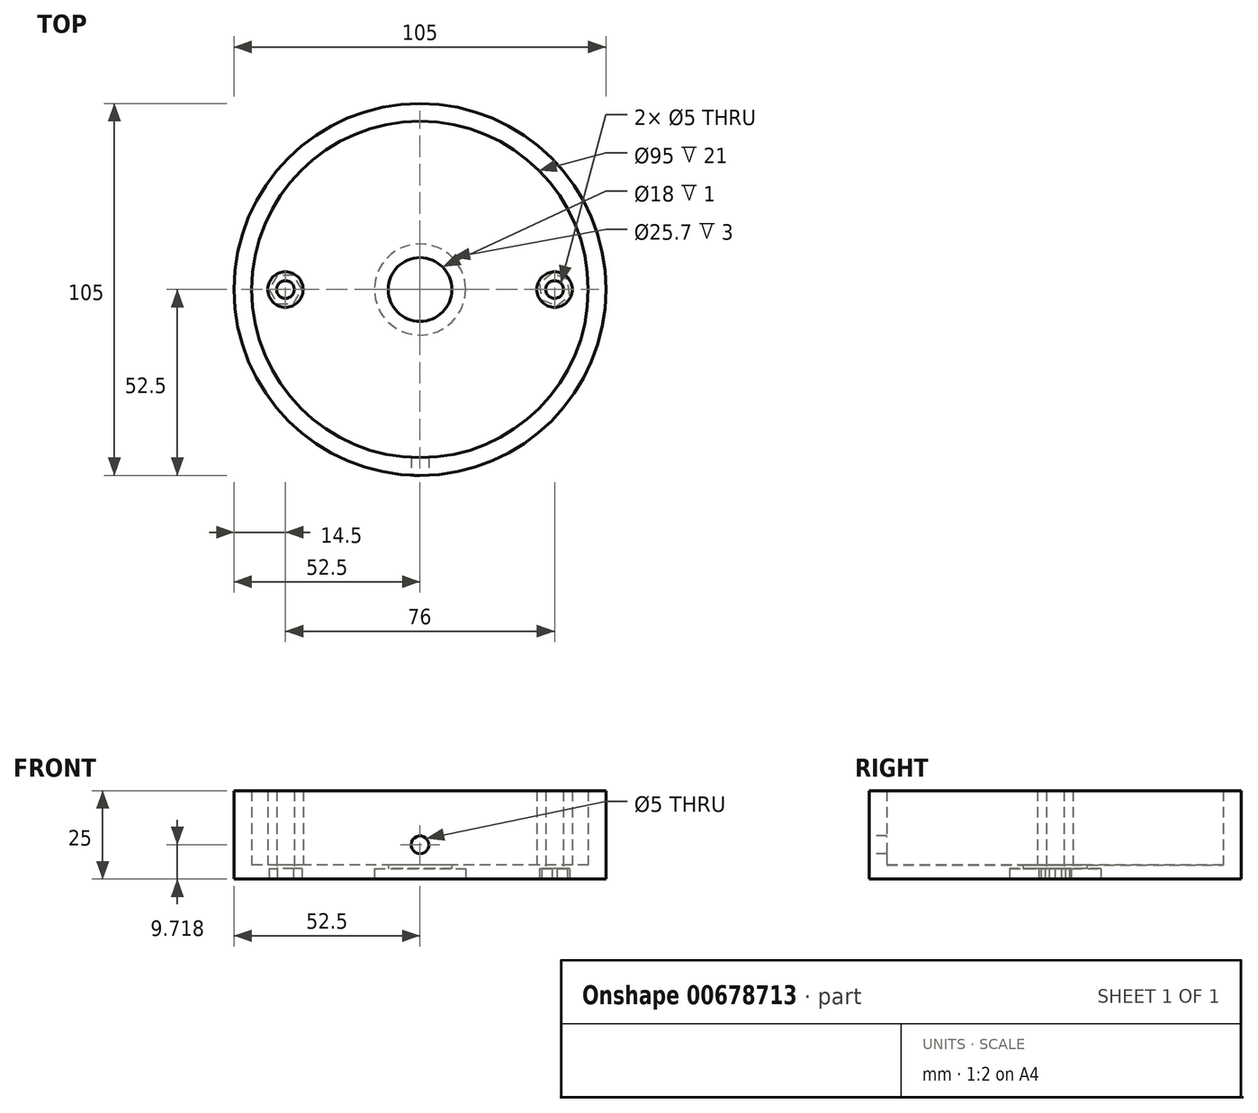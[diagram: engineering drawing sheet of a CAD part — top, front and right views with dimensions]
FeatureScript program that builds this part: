
annotation { "Feature Type Name" : "Feature", "Feature Type Description" : "" }
export const myFeature = defineFeature(function(context is Context, id is Id, definition is map)
    precondition{}
    {
        {
            var Q0;
            Q0=qCreatedBy(makeId("Top.planeOp"),FACE);
            var sketch = newSketch(context, id + "F0", { "sketchPlane" : qUnion([Q0])});
            skCircle(sketch, "E0", {"center": v(0, 0) * mm, "radius": 47.5 * mm});
            skCircle(sketch, "E1", {"center": v(0, 0) * mm, "radius": 52.5 * mm});
            skCircle(sketch, "E2", {"center": v(0, 0) * mm, "radius": 9 * mm});
            skPoint(sketch, "E3", {"position": v(38, 0) * mm});
            skCircle(sketch, "E4", {"center": v(38, 0) * mm, "radius": 2.5 * mm});
            skCircle(sketch, "E5", {"center": v(-38, 0) * mm, "radius": 2.5 * mm});
            skPoint(sketch, "E6", {"position": v(0, -30) * mm});
            skSolve(sketch);
        }
        {
            var Q0;
            Q0=makeQuery(id+"F0.imprint","IMPRINT",FACE,{"disambiguationData":[TD([[makeQuery(id+"F0.imprint","IMPRINT",EDGE,{"derivedFrom":sQuery(id+"F0.wireOp",EDGE,"E0")}),1.0]])]});
            extrude(context, id + "F1", {"entities" : qUnion([Q0]), "depth" : 4 * mm, "offsetDistance" : 25 * mm});
        }
        {
            var Q0;
            Q0=makeQuery(id+"F0.imprint","IMPRINT",FACE,{"disambiguationData":[TD([[makeQuery(id+"F0.imprint","IMPRINT",EDGE,{"derivedFrom":sQuery(id+"F0.wireOp",EDGE,"E0")}),-1.0]])]});
            extrude(context, id + "F2", {"entities" : qUnion([Q0]), "operationType" : NewBodyOperationType.ADD, "depth" : 22 * mm, "offsetDistance" : 25 * mm});
        }
        {
            var Q0;
            Q0 = qSketchRegion(id + "F0", true);
            extrude(context, id + "F3", {"entities" : qUnion([Q0]), "operationType" : NewBodyOperationType.ADD, "depth" : 25 * mm, "offsetDistance" : 25 * mm});
        }
        {
            var Q0;
            {var subQ0=sQuery(id+"F0.wireOp",EDGE,"KxPcmW6f-jrK5-NJJ2-CGSX-odAfUIyHA8Hz");var subQ1=sQuery(id+"F0.wireOp",EDGE,"Ce3efajX-mTEG-fQcQ-4AWC-PIJuVlCcTGQe");var subQ2=sQuery(id+"F0.wireOp",EDGE,"BphFqhMG-zdux-vk7n-OLHF-6ssDePMP9lv5");var subQ3=sQuery(id+"F0.wireOp",EDGE,"E0");Q0=makeQuery(id+"FwEDGeEJbmtDzLu_0.boolean.opBoolean","MERGE",FACE,{"derivedFrom":[makeQuery(id+"F2.boolean.opBoolean","MERGE",FACE,{"derivedFrom":[makeQuery(id+"F1.opExtrude","CAP_FACE",FACE,{"disambiguationData":[OSD([subQ3,sQuery(id+"F0.wireOp",EDGE,"B8NBj5N8-SaxT-broy-7EAl-QKT3yiHgvJLJ"),subQ2,subQ1,subQ0])],"isStart":true}),makeQuery(id+"F2.opExtrude","CAP_FACE",FACE,{"disambiguationData":[OSD([subQ3,sQuery(id+"F0.wireOp",EDGE,"E1")])],"isStart":true})]}),makeQuery(id+"FwEDGeEJbmtDzLu_0.opExtrude","CAP_FACE",FACE,{"disambiguationData":[OSD([sQuery(id+"F0.wireOp",EDGE,"WK8yWc9G-alHI-a11c-cyK7-Gcr48cerju4L"),subQ2])],"isStart":true}),makeQuery(id+"FwEDGeEJbmtDzLu_0.opExtrude","CAP_FACE",FACE,{"disambiguationData":[OSD([sQuery(id+"F0.wireOp",EDGE,"opKP8o53-cgpy-PRBC-jVus-ZTeZxwGO5yKw"),subQ1])],"isStart":true}),makeQuery(id+"FwEDGeEJbmtDzLu_0.opExtrude","CAP_FACE",FACE,{"disambiguationData":[OSD([sQuery(id+"F0.wireOp",EDGE,"vjQTa54q-FzXU-Qp47-7nQK-FbvYVxZVb2CL"),subQ0])],"isStart":true})]});}
            var sketch = newSketch(context, id + "F4", { "sketchPlane" : qUnion([Q0])});
            skSolve(sketch);
        }
        {
            var Q0;
            {var subQ0=sQuery(id+"F0.wireOp",EDGE,"KxPcmW6f-jrK5-NJJ2-CGSX-odAfUIyHA8Hz");var subQ1=sQuery(id+"F0.wireOp",EDGE,"Ce3efajX-mTEG-fQcQ-4AWC-PIJuVlCcTGQe");var subQ2=sQuery(id+"F0.wireOp",EDGE,"BphFqhMG-zdux-vk7n-OLHF-6ssDePMP9lv5");var subQ3=sQuery(id+"F0.wireOp",EDGE,"E0");Q0=makeQuery(id+"FwEDGeEJbmtDzLu_0.boolean.opBoolean","MERGE",FACE,{"derivedFrom":[makeQuery(id+"F2.boolean.opBoolean","MERGE",FACE,{"derivedFrom":[makeQuery(id+"F1.opExtrude","CAP_FACE",FACE,{"disambiguationData":[OSD([subQ3,sQuery(id+"F0.wireOp",EDGE,"B8NBj5N8-SaxT-broy-7EAl-QKT3yiHgvJLJ"),subQ2,subQ1,subQ0])],"isStart":true}),makeQuery(id+"F2.opExtrude","CAP_FACE",FACE,{"disambiguationData":[OSD([subQ3,sQuery(id+"F0.wireOp",EDGE,"E1")])],"isStart":true})]}),makeQuery(id+"FwEDGeEJbmtDzLu_0.opExtrude","CAP_FACE",FACE,{"disambiguationData":[OSD([sQuery(id+"F0.wireOp",EDGE,"WK8yWc9G-alHI-a11c-cyK7-Gcr48cerju4L"),subQ2])],"isStart":true}),makeQuery(id+"FwEDGeEJbmtDzLu_0.opExtrude","CAP_FACE",FACE,{"disambiguationData":[OSD([sQuery(id+"F0.wireOp",EDGE,"opKP8o53-cgpy-PRBC-jVus-ZTeZxwGO5yKw"),subQ1])],"isStart":true}),makeQuery(id+"FwEDGeEJbmtDzLu_0.opExtrude","CAP_FACE",FACE,{"disambiguationData":[OSD([sQuery(id+"F0.wireOp",EDGE,"vjQTa54q-FzXU-Qp47-7nQK-FbvYVxZVb2CL"),subQ0])],"isStart":true})]});}
            var sketch = newSketch(context, id + "F5", { "sketchPlane" : qUnion([Q0])});
            skCircle(sketch, "E7", {"center": v(0, 0) * mm, "radius": 12.85 * mm});
            skSolve(sketch);
        }
        {
            var Q0;
            Q0=makeQuery(id+"F5.imprint","IMPRINT",FACE,{"disambiguationData":[TD([[makeQuery(id+"F5.imprint","IMPRINT",EDGE,{"derivedFrom":sQuery(id+"F5.wireOp",EDGE,"E7")}),1.0]])]});
            extrude(context, id + "F6", {"entities" : qUnion([Q0]), "operationType" : NewBodyOperationType.REMOVE, "oppositeDirection" : true, "depth" : 3 * mm, "offsetDistance" : 25 * mm});
        }
        {
            var Q0;
            Q0=makeQuery(id+"F4.imprint","IMPRINT",FACE,{"disambiguationData":[TD([[makeQuery(id+"F4.imprint","IMPRINT",EDGE,{"derivedFrom":makeQuery(id+"F1.opExtrude","CAP_EDGE",EDGE,{"disambiguationData":[OSD([sQuery(id+"F0.wireOp",EDGE,"E2")])],"isStart":true})}),1.0]])]});
            var sketch = newSketch(context, id + "F7", { "sketchPlane" : qUnion([Q0])});
            skPoint(sketch, "E8", {"position": v(-38, 0) * mm});
            skPoint(sketch, "E9", {"position": v(0, 0) * mm});
            skPoint(sketch, "E10", {"position": v(38, 0) * mm});
            skLineSegment(sketch, "E11.0", {"start": v(-35.7, -4) * mm, "end": v(-40.3, -4) * mm});
            skLineSegment(sketch, "E11.1", {"start": v(-40.3, -4) * mm, "end": v(-42.62, 0) * mm});
            skLineSegment(sketch, "E11.2", {"start": v(-42.62, 0) * mm, "end": v(-40.3, 4) * mm});
            skLineSegment(sketch, "E11.3", {"start": v(-40.3, 4) * mm, "end": v(-35.7, 4) * mm});
            skLineSegment(sketch, "E11.4", {"start": v(-35.7, 4) * mm, "end": v(-33.38, 0) * mm});
            skLineSegment(sketch, "E11.5", {"start": v(-33.38, 0) * mm, "end": v(-35.7, -4) * mm});
            skPoint(sketch, "E11.0.midPoint", {"position": v(-38, -4) * mm});
            skLineSegment(sketch, "E12.0", {"start": v(41.62, -2.87) * mm, "end": v(37.32, -4.57) * mm});
            skLineSegment(sketch, "E12.1", {"start": v(37.32, -4.57) * mm, "end": v(33.7, -1.7) * mm});
            skLineSegment(sketch, "E12.2", {"start": v(33.7, -1.7) * mm, "end": v(34.38, 2.87) * mm});
            skLineSegment(sketch, "E12.3", {"start": v(34.38, 2.87) * mm, "end": v(38.68, 4.57) * mm});
            skLineSegment(sketch, "E12.4", {"start": v(38.68, 4.57) * mm, "end": v(42.3, 1.7) * mm});
            skLineSegment(sketch, "E12.5", {"start": v(42.3, 1.7) * mm, "end": v(41.62, -2.87) * mm});
            skPoint(sketch, "E12.0.midPoint", {"position": v(39.47, -3.72) * mm});
            skSolve(sketch);
        }
        {
            var Q0;
            Q0=makeQuery(id+"F7.imprint","IMPRINT",FACE,{"disambiguationData":[TD([[makeQuery(id+"F7.imprint","IMPRINT",EDGE,{"derivedFrom":sQuery(id+"F7.wireOp",EDGE,"E12.0")}),-1.0]])]});
            var Q1;
            Q1=makeQuery(id+"F7.imprint","IMPRINT",FACE,{"disambiguationData":[TD([[makeQuery(id+"F7.imprint","IMPRINT",EDGE,{"derivedFrom":sQuery(id+"F7.wireOp",EDGE,"E11.0")}),-1.0]])]});
            extrude(context, id + "F8", {"entities" : qUnion([Q0, Q1]), "operationType" : NewBodyOperationType.REMOVE, "oppositeDirection" : true, "depth" : 3 * mm, "offsetDistance" : 25 * mm});
        }
        {
            var Q0;
            Q0=makeQuery(id+"F1.opExtrude","CAP_FACE",FACE,{"disambiguationData":[OSD([sQuery(id+"F0.wireOp",EDGE,"E0"),sQuery(id+"F0.wireOp",EDGE,"E2"),sQuery(id+"F0.wireOp",EDGE,"E4"),sQuery(id+"F0.wireOp",EDGE,"E5")])],"isStart":false});
            var sketch = newSketch(context, id + "F9", { "sketchPlane" : qUnion([Q0])});
            skCircle(sketch, "E13", {"center": v(-38, 0) * mm, "radius": 5 * mm});
            skCircle(sketch, "E14", {"center": v(38, 0) * mm, "radius": 5 * mm});
            skSolve(sketch);
        }
        {
            var Q0;
            Q0=makeQuery(id+"F9.imprint","IMPRINT",FACE,{"disambiguationData":[TD([[makeQuery(id+"F9.imprint","IMPRINT",EDGE,{"derivedFrom":makeQuery(id+"F1.opExtrude","CAP_EDGE",EDGE,{"disambiguationData":[OSD([sQuery(id+"F0.wireOp",EDGE,"E4")])],"isStart":false})}),1.0]])]});
            var Q1;
            Q1=makeQuery(id+"F9.imprint","IMPRINT",FACE,{"disambiguationData":[TD([[makeQuery(id+"F9.imprint","IMPRINT",EDGE,{"derivedFrom":makeQuery(id+"F1.opExtrude","CAP_EDGE",EDGE,{"disambiguationData":[OSD([sQuery(id+"F0.wireOp",EDGE,"E5")])],"isStart":false})}),1.0]])]});
            var Q2;
            Q2=makeQuery(id+"F9.imprint","IMPRINT",FACE,{"disambiguationData":[TD([[makeQuery(id+"F9.imprint","IMPRINT",EDGE,{"derivedFrom":sQuery(id+"F9.wireOp",EDGE,"E14")}),1.0]])]});
            var Q3;
            Q3=makeQuery(id+"F9.imprint","IMPRINT",FACE,{"disambiguationData":[TD([[makeQuery(id+"F9.imprint","IMPRINT",EDGE,{"derivedFrom":sQuery(id+"F9.wireOp",EDGE,"E13")}),1.0]])]});
            extrude(context, id + "F10", {"entities" : qUnion([Q0, Q1, Q2, Q3]), "operationType" : NewBodyOperationType.ADD, "depth" : 21 * mm, "offsetDistance" : 25 * mm});
        }
        {
            var Q0;
            Q0=makeQuery(id+"F4.imprint","IMPRINT",FACE,{"disambiguationData":[TD([[makeQuery(id+"F4.imprint","IMPRINT",EDGE,{"derivedFrom":makeQuery(id+"F1.opExtrude","CAP_EDGE",EDGE,{"disambiguationData":[OSD([sQuery(id+"F0.wireOp",EDGE,"E5")])],"isStart":true})}),-1.0]])]});
            var Q1;
            Q1=makeQuery(id+"F4.imprint","IMPRINT",FACE,{"disambiguationData":[TD([[makeQuery(id+"F4.imprint","IMPRINT",EDGE,{"derivedFrom":makeQuery(id+"F1.opExtrude","CAP_EDGE",EDGE,{"disambiguationData":[OSD([sQuery(id+"F0.wireOp",EDGE,"E4")])],"isStart":true})}),-1.0]])]});
            extrude(context, id + "F11", {"entities" : qUnion([Q0, Q1]), "operationType" : NewBodyOperationType.REMOVE, "oppositeDirection" : true, "depth" : 30 * mm, "offsetDistance" : 25 * mm});
        }
        {
            var Q0;
            Q0=qCreatedBy(makeId("Front.planeOp"),FACE);
            var Q1;
            Q1 = qBodyType(qCreatedBy(id + "F13" ,EDGE), BodyType.WIRE);
            cPlane(context, id + "F12", {"entities" : qUnion([Q0, Q1]), "cplaneType" : CPlaneType.OFFSET, "offset" : 52.7 * mm, "width" : 150 * mm, "height" : 150 * mm});
        }
        {
            var Q0;
            Q0=qCreatedBy(id+"F12.planeOp",FACE);
            var sketch = newSketch(context, id + "F13", { "sketchPlane" : qUnion([Q0])});
            skPoint(sketch, "E15", {"position": v(0, 9.72) * mm});
            skSolve(sketch);
        }
        {
            var Q0;
            Q0=sQuery(id+"F13.wireOp",VERTEX,"E15");
            var Q1;
            Q1=makeQuery(id+"F1.opExtrude","SWEPT_BODY",BODY,{"disambiguationData":[OSD([sQuery(id+"F0.wireOp",EDGE,"E0"),sQuery(id+"F0.wireOp",EDGE,"E2"),sQuery(id+"F0.wireOp",EDGE,"E4"),sQuery(id+"F0.wireOp",EDGE,"E5")])]});
            hole(context, id + "F14", {"style" : HoleStyle.SIMPLE, "endStyle" : HoleEndStyle.BLIND, "holeDiameter" : 5 * mm, "majorDiameter" : 5 * mm, "holeDepth" : 10 * mm, "isTappedThrough" : true, "tappedDepth" : 12 * mm, "tapClearance" : 3, "locations" : qUnion([Q0]), "scope" : qUnion([Q1])});
        }
    });
